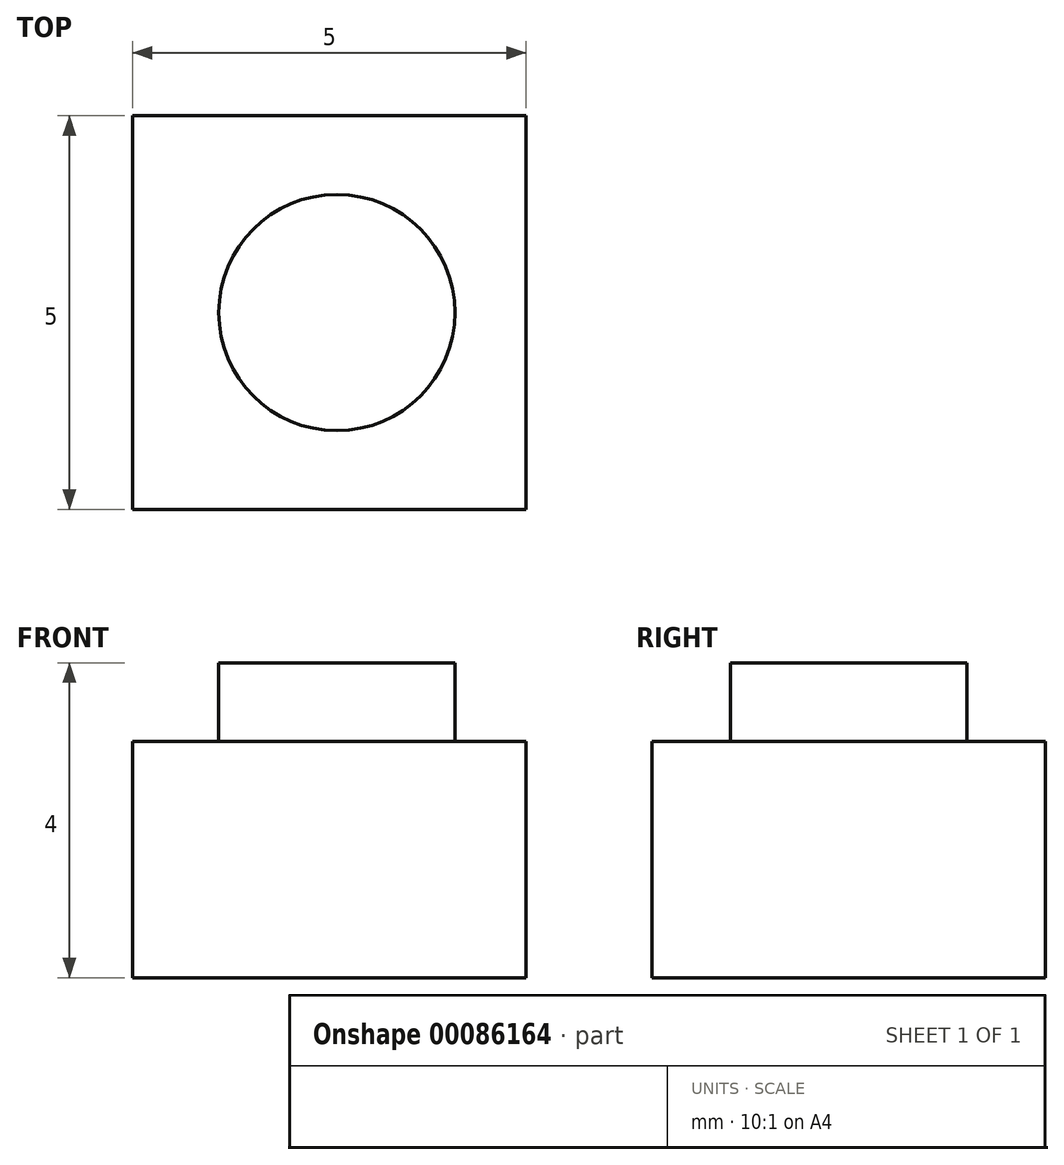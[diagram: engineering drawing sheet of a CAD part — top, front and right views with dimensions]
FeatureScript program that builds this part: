
annotation { "Feature Type Name" : "Feature", "Feature Type Description" : "" }
export const myFeature = defineFeature(function(context is Context, id is Id, definition is map)
    precondition{}
    {
        {
            var Q0;
            Q0=qCreatedBy(makeId("Top.planeOp"),FACE);
            var sketch = newSketch(context, id + "F0", { "sketchPlane" : qUnion([Q0])});
            skLineSegment(sketch, "E0.bottom", {"start": v(0, 38.02) * mm, "end": v(5, 38.02) * mm});
            skLineSegment(sketch, "E0.top", {"start": v(0, 33.02) * mm, "end": v(5, 33.02) * mm});
            skLineSegment(sketch, "E0.left", {"start": v(0, 38.02) * mm, "end": v(0, 33.02) * mm});
            skLineSegment(sketch, "E0.right", {"start": v(5, 38.02) * mm, "end": v(5, 33.02) * mm});
            skCircle(sketch, "E1", {"center": v(2.6, 35.52) * mm, "radius": 1.5 * mm});
            skPoint(sketch, "E1.centerSnap0", {"position": v(0, 35.52) * mm});
            skSolve(sketch);
        }
        {
            var Q0;
            Q0 = qSketchRegion(id + "F0", true);
            var Q1;
            Q1=makeQuery(id+"F0.imprint","IMPRINT",FACE,{"disambiguationData":[TD([[makeQuery(id+"F0.imprint","IMPRINT",EDGE,{"derivedFrom":sQuery(id+"F0.wireOp",EDGE,"E0.bottom")}),-1.0]])]});
            var Q2;
            Q2=makeQuery(id+"F0.imprint","IMPRINT",FACE,{"disambiguationData":[TD([[makeQuery(id+"F0.imprint","IMPRINT",EDGE,{"derivedFrom":sQuery(id+"F0.wireOp",EDGE,"E1")}),1.0]])]});
            extrude(context, id + "F1", {"entities" : qUnion([Q0, Q1, Q2]), "depth" : 3 * mm, "offsetDistance" : 25 * mm});
        }
        {
            var Q0;
            Q0=makeQuery(id+"F0.imprint","IMPRINT",FACE,{"disambiguationData":[TD([[makeQuery(id+"F0.imprint","IMPRINT",EDGE,{"derivedFrom":sQuery(id+"F0.wireOp",EDGE,"E1")}),1.0]])]});
            extrude(context, id + "F2", {"entities" : qUnion([Q0]), "operationType" : NewBodyOperationType.ADD, "depth" : 4 * mm, "offsetDistance" : 25 * mm});
        }
    });
